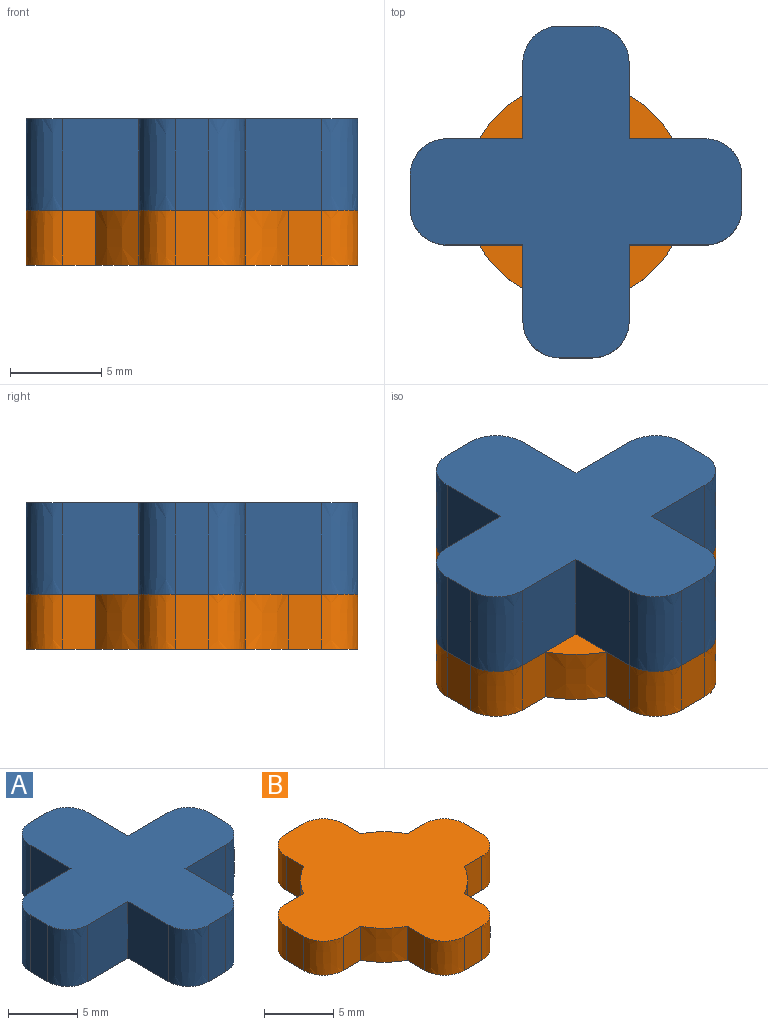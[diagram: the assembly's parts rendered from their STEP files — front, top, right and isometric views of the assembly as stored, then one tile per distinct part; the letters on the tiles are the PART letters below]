
ASSEMBLY  parts=2 mates=1
PART A: 22 faces, bbox 18.1x18.1x5 mm
  f0: plane 5x4.17mm, normal (-1,0,0), area 20.8mm2, adj f1,f19,f20,f21
  f1: extruded ~5x2mm, area 15.7mm2, adj f0,f2,f20,f21
  f2: plane 5x1.81mm, normal (0,-1,0), area 9mm2, adj f1,f3,f20,f21
  f3: extruded ~5x2mm, area 15.7mm2, adj f2,f4,f20,f21
  f4: plane 5x4.17mm, normal (1,0,0), area 20.8mm2, adj f3,f5,f20,f21
  f5: plane 5x4.17mm, normal (0,-1,0), area 20.8mm2, adj f4,f6,f20,f21
  f6: extruded ~5x2mm, area 15.7mm2, adj f5,f7,f20,f21
  f7: plane 5x1.81mm, normal (1,0,0), area 9mm2, adj f6,f8,f20,f21
  f8: extruded ~5x2mm, area 15.7mm2, adj f7,f9,f20,f21
  f9: plane 5x4.17mm, normal (0,1,0), area 20.8mm2, adj f8,f10,f20,f21
  f10: plane 5x4.17mm, normal (1,0,0), area 20.8mm2, adj f9,f11,f20,f21
  f11: extruded ~5x2mm, area 15.7mm2, adj f10,f12,f20,f21
  f12: plane 5x1.81mm, normal (0,1,0), area 9mm2, adj f11,f13,f20,f21
  f13: extruded ~5x2mm, area 15.7mm2, adj f12,f14,f20,f21
  f14: plane 5x4.17mm, normal (-1,0,0), area 20.8mm2, adj f13,f15,f20,f21
  f15: plane 5x4.17mm, normal (0,1,0), area 20.8mm2, adj f14,f16,f20,f21
  f16: extruded ~5x2mm, area 15.7mm2, adj f15,f17,f20,f21
  f17: plane 5x1.81mm, normal (-1,0,0), area 9mm2, adj f16,f18,f20,f21
  f18: extruded ~5x2mm, area 15.7mm2, adj f17,f19,f20,f21
  f19: plane 5x4.17mm, normal (0,-1,0), area 20.8mm2, adj f0,f18,f20,f21
  f20: plane 18.14x18.14mm, normal (0,0,1), area 170mm2, adj f0,f1,f2,f3,f4,f5,f6,f7
  f21: plane 18.14x18.14mm, normal (0,0,-1), area 170mm2, adj f0,f1,f2,f3,f4,f5,f6,f7
PART B: 26 faces, bbox 18.1x18.1x3 mm
  f0: plane 3x1.81mm, normal (-1,0,0), area 5.4mm2, adj f1,f23,f24,f25
  f1: extruded ~3x2mm, area 9.4mm2, adj f0,f2,f24,f25
  f2: plane 3x1.79mm, normal (0,-1,0), area 5.4mm2, adj f1,f3,f24,f25
  f3: extruded ~3x2.38mm, area 10.2mm2, adj f2,f4,f24,f25
  f4: plane 3x1.79mm, normal (-1,0,0), area 5.4mm2, adj f3,f5,f24,f25
  f5: extruded ~3x2mm, area 9.4mm2, adj f4,f6,f24,f25
  f6: plane 3x1.81mm, normal (0,-1,0), area 5.4mm2, adj f5,f7,f24,f25
  f7: extruded ~3x2mm, area 9.4mm2, adj f6,f8,f24,f25
  f8: plane 3x1.79mm, normal (1,0,0), area 5.4mm2, adj f7,f9,f24,f25
  f9: extruded ~3x2.38mm, area 10.2mm2, adj f8,f10,f24,f25
  f10: plane 3x1.79mm, normal (0,-1,0), area 5.4mm2, adj f9,f11,f24,f25
  f11: extruded ~3x2mm, area 9.4mm2, adj f10,f12,f24,f25
  f12: plane 3x1.81mm, normal (1,0,0), area 5.4mm2, adj f11,f13,f24,f25
  f13: extruded ~3x2mm, area 9.4mm2, adj f12,f14,f24,f25
  f14: plane 3x1.79mm, normal (0,1,0), area 5.4mm2, adj f13,f15,f24,f25
  f15: extruded ~3x2.37mm, area 10.2mm2, adj f14,f16,f24,f25
  f16: plane 3x1.79mm, normal (1,0,0), area 5.4mm2, adj f15,f17,f24,f25
  f17: extruded ~3x2mm, area 9.4mm2, adj f16,f18,f24,f25
  f18: plane 3x1.81mm, normal (0,1,0), area 5.4mm2, adj f17,f19,f24,f25
  f19: extruded ~3x2mm, area 9.4mm2, adj f18,f20,f24,f25
  f20: plane 3x1.79mm, normal (-1,0,0), area 5.4mm2, adj f19,f21,f24,f25
  f21: extruded ~3x2.37mm, area 10.2mm2, adj f20,f22,f24,f25
  f22: plane 3x1.79mm, normal (0,1,0), area 5.4mm2, adj f21,f23,f24,f25
  f23: extruded ~3x2mm, area 9.4mm2, adj f0,f22,f24,f25
  f24: plane 18.14x18.14mm, normal (0,0,1), area 183.4mm2, adj f0,f1,f2,f3,f4,f5,f6,f7
  f25: plane 18.14x18.14mm, normal (0,0,-1), area 183.4mm2, adj f0,f1,f2,f3,f4,f5,f6,f7
PLACE A t=(130.84,-0.4,28.25)mm
PLACE B t=(-0.78,4.43,25.25)mm
MATE fastened A.f21 <-> B.f24  axis (0,0,-1) through (75.59,38.85,28.25)mm
